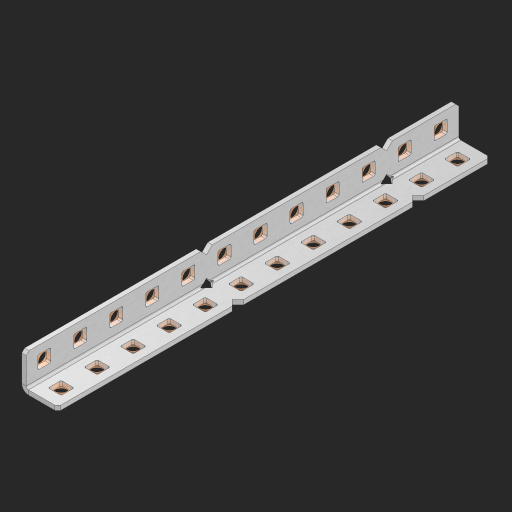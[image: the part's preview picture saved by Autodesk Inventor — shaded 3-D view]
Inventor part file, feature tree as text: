
AUTODESK INVENTOR PART (.ipt)
format: ipt  version: 2023 (Build 270158000, 158)  size: 651,776 bytes
history: native  units: in
note: dims shown in document units (in); Inventor stores cm internally (conversion verified against a paired STEP export)
features: other x30, extrude x25, sheet_metal_op x8, sketch x5, pattern_linear x1, mirror x1, chamfer x1
ambient origin geometry x8: Origin, YZ Plane, XZ Plane, XY Plane, X Axis, Y Axis, Z Axis, Center Point
bodies: Solid1 (feature_tree), Body (feature_tree)
feature tree (71):
  sheet_metal_op  "Flanges"
  sheet_metal_op  "Body Pattern"
  other  "Arc Length"
  pattern_linear  "Notch Pattern"  Spacing1=0.125in  [1 undecoded]
  other  "Diagonal Plane"
  mirror  "Everything Mirrored"
  chamfer  "End Chamfer"
  sketch  "Sketch1"  dims[d0=0.5in]
  other  "Plate1"
  sketch  "Sketch2"  dims[d1=6.0in]
  other  "Plate2"
  sheet_metal_op  "Bend1"
  sheet_metal_op  "Corner1"
  sketch  "Sketch8"  dims[d2=0.0625in]
  sketch  "Sketch9"  dims[d3=0.0625in]
  other  "Srf91"
  sheet_metal_op  "Body Pattern Sketch"
  other  "Srf92"
  sketch  "Sketch13"  dims[d4=0.0312in d5=0.125in d6=0.0625in d7=0.5in d8=90.0deg d9=0.0312in d10=0.25in d11=0.0625in d12=0.0625in d49=0.182in d50=0.02in d52=0.25in d53=0.0625in d54=0.0in d55=0.172in d56=1.0in d57=0.0in d85=0.1473in d86=0.1782in d89=0.0625in d90=0.0in d91=0.04in d92=0.0491in d95=2.5in d96=0.04in d97=0.25in d98=45.0deg d123=0.204in d126=0.0491in d127=0.1473in d128=0.08in d129=0.04in d130=2.5in d131=4.7244in d133=0.5in d134=0.3937in d136=1.0in]
  other  "Srf856"
  other  "Srf857"
  other  "Srf858"
  other  "Srf859"
  other  "Srf860"
  other  "Srf861"
  other  "Srf1275"
  other  "Srf1276"
  other  "Srf1278"
  other  "Srf1279"
  other  "Srf1280"
  other  "Srf1281"
  other  "Srf1282"
  other  "Srf1283"
  other  "Srf1383"
  other  "Srf1384"
  other  "Srf1385"
  other  "Srf1386"
  other  "Srf1387"
  other  "Srf1475"
  other  "Srf1476"
  other  "Srf1477"
  other  "Srf1478"
  other  "Srf1479"
  sheet_metal_op  "Body Stamp"
  sheet_metal_op  "Body Circle"
  sheet_metal_op  "Notch"
  extrude  "ExtrusionSrf92"  Depth=0.0625in
  extrude  "ExtrusionSrf856"  Depth=0.5in TaperAngle=90.0deg
  extrude  "ExtrusionSrf857"  Depth=0.25in
  extrude  "ExtrusionSrf858"  Depth=0.0625in
  extrude  "ExtrusionSrf859"  Depth=0.0625in
  extrude  "ExtrusionSrf860"  Depth=0.3937in
  extrude  "ExtrusionSrf861"  Depth=0.02in
  extrude  "ExtrusionSrf1275"  Depth=0.25in
  extrude  "ExtrusionSrf1276"  Depth=0.0625in
  extrude  "ExtrusionSrf1277"  TaperAngle=0.0deg  [1 undecoded]
  extrude  "ExtrusionSrf1278"  Depth=0.3937in
  extrude  "ExtrusionSrf1279"  Depth=0.3937in TaperAngle=0.0deg
  extrude  "ExtrusionSrf1280"  Depth=0.3937in
  extrude  "ExtrusionSrf1281"  Depth=0.3937in
  extrude  "ExtrusionSrf1282"  Depth=0.0625in
  extrude  "ExtrusionSrf1383"  Depth=0.3937in TaperAngle=0.0deg
  extrude  "ExtrusionSrf1384"  Depth=0.3937in
  extrude  "ExtrusionSrf1385"  Depth=0.25in TaperAngle=45.0deg
  extrude  "ExtrusionSrf1386"  Depth=0.3937in
  extrude  "ExtrusionSrf1387"  Depth=0.3937in
  extrude  "ExtrusionSrf1475"  Depth=0.3937in
  extrude  "ExtrusionSrf1476"  Depth=0.3937in
  extrude  "ExtrusionSrf1477"  Depth=0.3937in
  extrude  "ExtrusionSrf1478"  Depth=0.3937in
  extrude  "ExtrusionSrf1479"  Depth=0.3937in
note: 2 required parameter values undecoded (feature->parameter linkage not recoverable at this tier; creation-order binding heuristic only, values carry confidence <= 0.55)
